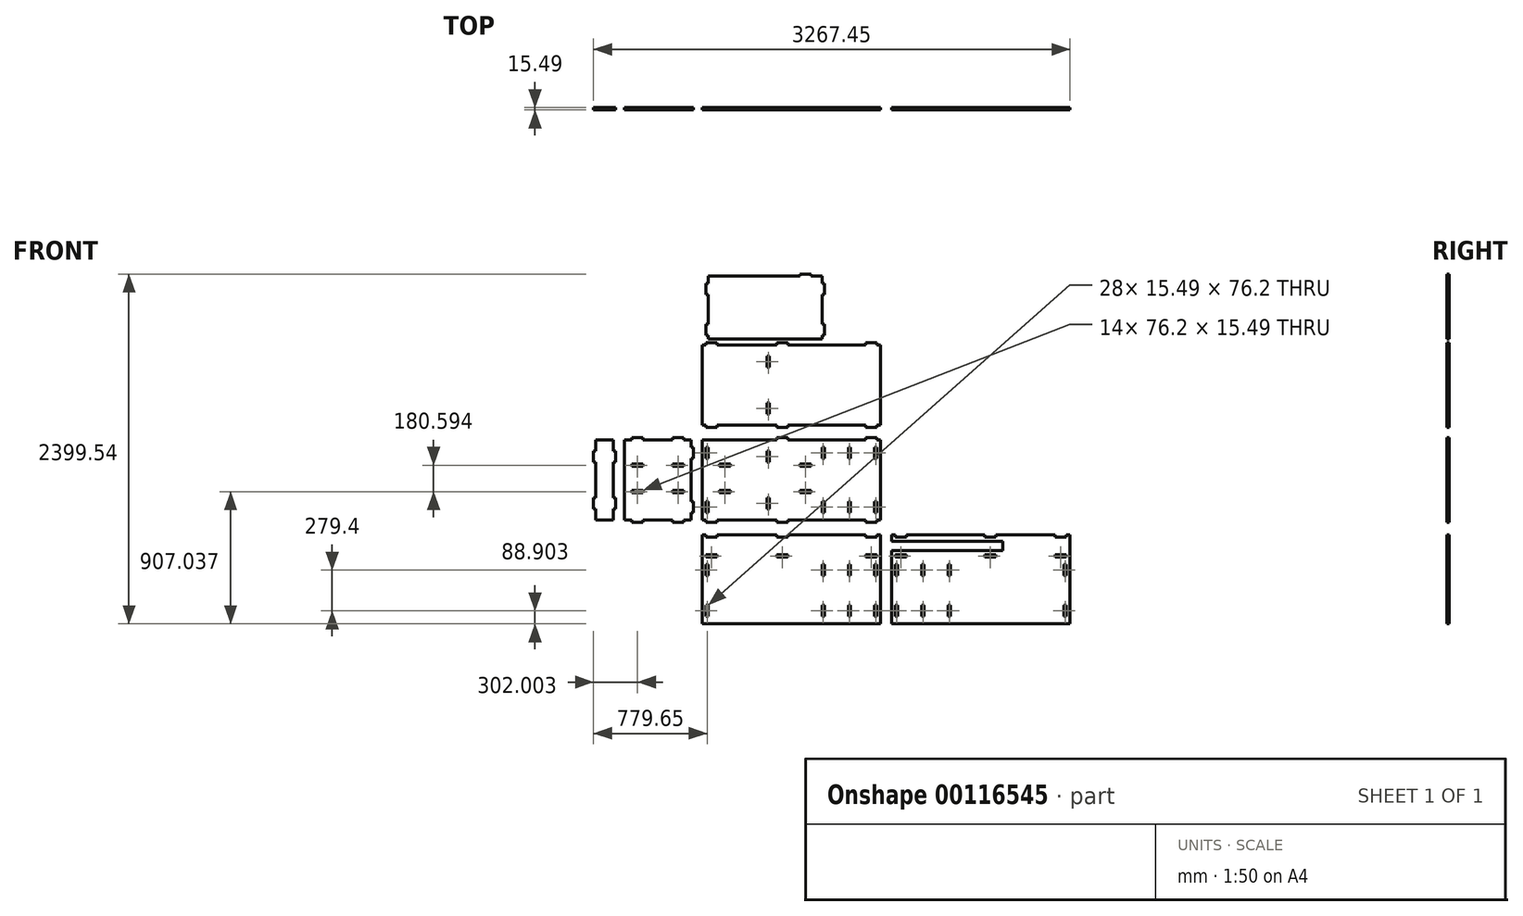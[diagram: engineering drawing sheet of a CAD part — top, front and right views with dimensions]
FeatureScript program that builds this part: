
annotation { "Feature Type Name" : "Feature", "Feature Type Description" : "" }
export const myFeature = defineFeature(function(context is Context, id is Id, definition is map)
    precondition{}
    {
        {
            var Q0;
            Q0=qCreatedBy(makeId("Front.planeOp"),FACE);
            var sketch = newSketch(context, id + "F0", { "sketchPlane" : qUnion([Q0])});
            skLineSegment(sketch, "E0.bottom", {"start": v(611.19, 274.64) * mm, "end": v(-611.19, 274.64) * mm});
            skLineSegment(sketch, "E0.top", {"start": v(611.19, -274.64) * mm, "end": v(-611.19, -274.64) * mm});
            skLineSegment(sketch, "E0.left", {"start": v(611.19, 274.64) * mm, "end": v(611.19, -274.64) * mm});
            skLineSegment(sketch, "E0.right", {"start": v(-611.19, 274.64) * mm, "end": v(-611.19, -274.64) * mm});
            skPoint(sketch, "E0.middle", {"position": v(0, 0) * mm});
            skLineSegment(sketch, "E1", {"start": v(0, 274.64) * mm, "end": v(0, -274.64) * mm, "construction": true});
            skLineSegment(sketch, "E2", {"start": v(-611.19, 0) * mm, "end": v(0, 0) * mm, "construction": true});
            skLineSegment(sketch, "E3", {"start": v(-305.6, -274.64) * mm, "end": v(-305.6, 274.64) * mm, "construction": true});
            skPoint(sketch, "E3.startSnap0", {"position": v(-305.6, 0) * mm});
            skLineSegment(sketch, "E4.bottom", {"start": v(-570.3, 223.84) * mm, "end": v(-585.79, 223.84) * mm});
            skLineSegment(sketch, "E4.top", {"start": v(-570.3, 147.64) * mm, "end": v(-585.79, 147.64) * mm});
            skLineSegment(sketch, "E4.left", {"start": v(-570.3, 223.84) * mm, "end": v(-570.3, 147.64) * mm});
            skLineSegment(sketch, "E4.right", {"start": v(-585.79, 223.84) * mm, "end": v(-585.79, 147.64) * mm});
            skLineSegment(sketch, "E5.MirrorCS", {"start": v(-570.3, -223.84) * mm, "end": v(-570.3, -147.64) * mm});
            skLineSegment(sketch, "E6.MirrorCS", {"start": v(-585.79, -223.84) * mm, "end": v(-585.79, -147.64) * mm});
            skLineSegment(sketch, "E7.MirrorCS", {"start": v(-570.3, -147.64) * mm, "end": v(-585.79, -147.64) * mm});
            skLineSegment(sketch, "E8.MirrorCS", {"start": v(-570.3, -223.84) * mm, "end": v(-585.79, -223.84) * mm});
            skLineSegment(sketch, "E9.MirrorCS", {"start": v(570.3, -223.84) * mm, "end": v(585.79, -223.84) * mm});
            skLineSegment(sketch, "E10.MirrorCS", {"start": v(570.3, -147.64) * mm, "end": v(585.79, -147.64) * mm});
            skLineSegment(sketch, "E11.MirrorCS", {"start": v(570.3, 223.84) * mm, "end": v(585.79, 223.84) * mm});
            skLineSegment(sketch, "E12.MirrorCS", {"start": v(570.3, 147.64) * mm, "end": v(585.79, 147.64) * mm});
            skLineSegment(sketch, "E13.MirrorCS", {"start": v(570.3, 223.84) * mm, "end": v(570.3, 147.64) * mm});
            skLineSegment(sketch, "E14.MirrorCS", {"start": v(585.79, 223.84) * mm, "end": v(585.79, 147.64) * mm});
            skLineSegment(sketch, "E15.MirrorCS", {"start": v(585.79, -223.84) * mm, "end": v(585.79, -147.64) * mm});
            skLineSegment(sketch, "E16.MirrorCS", {"start": v(570.3, -223.84) * mm, "end": v(570.3, -147.64) * mm});
            skLineSegment(sketch, "E17.bottom", {"start": v(-687.39, 274.64) * mm, "end": v(-1144.59, 274.64) * mm});
            skLineSegment(sketch, "E17.top", {"start": v(-687.39, -274.64) * mm, "end": v(-1144.59, -274.64) * mm});
            skLineSegment(sketch, "E17.left", {"start": v(-687.39, 274.64) * mm, "end": v(-687.39, -274.64) * mm});
            skLineSegment(sketch, "E17.right", {"start": v(-1144.59, 274.64) * mm, "end": v(-1144.59, -274.64) * mm});
            skLineSegment(sketch, "E18", {"start": v(-738.19, 274.64) * mm, "end": v(-738.19, 290.13) * mm});
            skLineSegment(sketch, "E19", {"start": v(-738.19, 290.13) * mm, "end": v(-814.39, 290.13) * mm});
            skLineSegment(sketch, "E20", {"start": v(-814.39, 290.13) * mm, "end": v(-814.39, 274.64) * mm});
            skLineSegment(sketch, "E21", {"start": v(-687.39, 223.84) * mm, "end": v(-671.9, 223.84) * mm});
            skLineSegment(sketch, "E22", {"start": v(-671.9, 223.84) * mm, "end": v(-671.9, 147.64) * mm});
            skLineSegment(sketch, "E23", {"start": v(-671.9, 147.64) * mm, "end": v(-687.39, 147.64) * mm});
            skLineSegment(sketch, "E24.MirrorCS", {"start": v(-687.39, -223.84) * mm, "end": v(-671.9, -223.84) * mm});
            skLineSegment(sketch, "E25.MirrorCS", {"start": v(-671.9, -147.64) * mm, "end": v(-687.39, -147.64) * mm});
            skLineSegment(sketch, "E26.MirrorCS", {"start": v(-671.9, -223.84) * mm, "end": v(-671.9, -147.64) * mm});
            skLineSegment(sketch, "E27", {"start": v(-915.99, 274.64) * mm, "end": v(-915.99, -274.64) * mm, "construction": true});
            skLineSegment(sketch, "E28.MirrorCS", {"start": v(-738.19, -274.64) * mm, "end": v(-738.19, -290.13) * mm});
            skLineSegment(sketch, "E29.MirrorCS", {"start": v(-814.39, -290.13) * mm, "end": v(-814.39, -274.64) * mm});
            skLineSegment(sketch, "E30.MirrorCS", {"start": v(-738.19, -290.13) * mm, "end": v(-814.39, -290.13) * mm});
            skLineSegment(sketch, "E31", {"start": v(-305.6, 223.84) * mm, "end": v(-305.6, -223.84) * mm, "construction": true});
            skPoint(sketch, "E32", {"position": v(-915.99, -279.72) * mm});
            skLineSegment(sketch, "E33.MirrorCS", {"start": v(-1017.59, -290.13) * mm, "end": v(-1017.59, -274.64) * mm});
            skLineSegment(sketch, "E34.MirrorCS", {"start": v(-1093.79, -290.13) * mm, "end": v(-1017.59, -290.13) * mm});
            skLineSegment(sketch, "E35.MirrorCS", {"start": v(-1093.79, -274.64) * mm, "end": v(-1093.79, -290.13) * mm});
            skLineSegment(sketch, "E36.MirrorCS", {"start": v(-1093.79, 274.64) * mm, "end": v(-1093.79, 290.13) * mm});
            skLineSegment(sketch, "E37.MirrorCS", {"start": v(-1093.79, 290.13) * mm, "end": v(-1017.59, 290.13) * mm});
            skLineSegment(sketch, "E38.MirrorCS", {"start": v(-1017.59, 290.13) * mm, "end": v(-1017.59, 274.64) * mm});
            skLineSegment(sketch, "E39", {"start": v(-611.19, 325.44) * mm, "end": v(611.19, 325.44) * mm, "construction": true});
            skLineSegment(sketch, "E40.MirrorCS", {"start": v(611.19, 376.24) * mm, "end": v(-611.19, 376.24) * mm});
            skLineSegment(sketch, "E41.MirrorCS", {"start": v(-611.19, 376.24) * mm, "end": v(-611.19, 925.51) * mm});
            skLineSegment(sketch, "E42.MirrorCS", {"start": v(611.19, 376.24) * mm, "end": v(611.19, 925.51) * mm});
            skLineSegment(sketch, "E43.MirrorCS", {"start": v(611.19, 925.51) * mm, "end": v(-611.19, 925.51) * mm});
            skLineSegment(sketch, "E44.bottom", {"start": v(-585.79, 274.64) * mm, "end": v(-509.59, 274.64) * mm});
            skLineSegment(sketch, "E44.top", {"start": v(-585.79, 290.13) * mm, "end": v(-509.59, 290.13) * mm});
            skLineSegment(sketch, "E44.left", {"start": v(-585.79, 274.64) * mm, "end": v(-585.79, 290.13) * mm});
            skLineSegment(sketch, "E44.right", {"start": v(-509.59, 274.64) * mm, "end": v(-509.59, 290.13) * mm});
            skLineSegment(sketch, "E45.MirrorCS", {"start": v(-25.4, 274.64) * mm, "end": v(-25.4, 290.13) * mm});
            skLineSegment(sketch, "E46.MirrorCS", {"start": v(-25.4, 290.13) * mm, "end": v(-101.6, 290.13) * mm});
            skLineSegment(sketch, "E47.MirrorCS", {"start": v(-101.6, 274.64) * mm, "end": v(-101.6, 290.13) * mm});
            skLineSegment(sketch, "E48.MirrorCS", {"start": v(585.79, 274.64) * mm, "end": v(585.79, 290.13) * mm});
            skLineSegment(sketch, "E49.MirrorCS", {"start": v(585.79, 290.13) * mm, "end": v(509.59, 290.13) * mm});
            skLineSegment(sketch, "E50.MirrorCS", {"start": v(509.59, 274.64) * mm, "end": v(509.59, 290.13) * mm});
            skLineSegment(sketch, "E51.MirrorCS", {"start": v(25.4, 274.64) * mm, "end": v(25.4, 290.13) * mm, "construction": true});
            skLineSegment(sketch, "E52.MirrorCS", {"start": v(25.4, 290.13) * mm, "end": v(101.6, 290.13) * mm, "construction": true});
            skLineSegment(sketch, "E53.MirrorCS", {"start": v(101.6, 274.64) * mm, "end": v(101.6, 290.13) * mm, "construction": true});
            skLineSegment(sketch, "E54.MirrorCS", {"start": v(-25.4, -274.64) * mm, "end": v(-25.4, -290.13) * mm});
            skLineSegment(sketch, "E55.MirrorCS", {"start": v(509.59, -274.64) * mm, "end": v(509.59, -290.13) * mm});
            skLineSegment(sketch, "E56.MirrorCS", {"start": v(585.79, -274.64) * mm, "end": v(585.79, -290.13) * mm});
            skLineSegment(sketch, "E57.MirrorCS", {"start": v(101.6, -274.64) * mm, "end": v(101.6, -290.13) * mm, "construction": true});
            skLineSegment(sketch, "E58.MirrorCS", {"start": v(25.4, -274.64) * mm, "end": v(25.4, -290.13) * mm, "construction": true});
            skLineSegment(sketch, "E59.MirrorCS", {"start": v(-101.6, -274.64) * mm, "end": v(-101.6, -290.13) * mm});
            skLineSegment(sketch, "E60.MirrorCS", {"start": v(25.4, -290.13) * mm, "end": v(101.6, -290.13) * mm, "construction": true});
            skLineSegment(sketch, "E61.MirrorCS", {"start": v(585.79, -290.13) * mm, "end": v(509.59, -290.13) * mm});
            skLineSegment(sketch, "E62.MirrorCS", {"start": v(-25.4, -290.13) * mm, "end": v(-101.6, -290.13) * mm});
            skLineSegment(sketch, "E63.MirrorCS", {"start": v(-585.79, -274.64) * mm, "end": v(-585.79, -290.13) * mm});
            skLineSegment(sketch, "E64.MirrorCS", {"start": v(-585.79, -290.13) * mm, "end": v(-509.59, -290.13) * mm});
            skLineSegment(sketch, "E65.MirrorCS", {"start": v(-509.59, -274.64) * mm, "end": v(-509.59, -290.13) * mm});
            skLineSegment(sketch, "E66.MirrorCS", {"start": v(25.4, 376.24) * mm, "end": v(25.4, 360.74) * mm, "construction": true});
            skLineSegment(sketch, "E67.MirrorCS", {"start": v(-25.4, 376.24) * mm, "end": v(-25.4, 360.74) * mm});
            skLineSegment(sketch, "E68.MirrorCS", {"start": v(101.6, 376.24) * mm, "end": v(101.6, 360.74) * mm, "construction": true});
            skLineSegment(sketch, "E69.MirrorCS", {"start": v(585.79, 376.24) * mm, "end": v(585.79, 360.74) * mm});
            skLineSegment(sketch, "E70.MirrorCS", {"start": v(509.59, 376.24) * mm, "end": v(509.59, 360.74) * mm});
            skLineSegment(sketch, "E71.MirrorCS", {"start": v(-101.6, 376.24) * mm, "end": v(-101.6, 360.74) * mm});
            skLineSegment(sketch, "E72.MirrorCS", {"start": v(-25.4, 360.74) * mm, "end": v(-101.6, 360.74) * mm});
            skLineSegment(sketch, "E73.MirrorCS", {"start": v(585.79, 360.74) * mm, "end": v(509.59, 360.74) * mm});
            skLineSegment(sketch, "E74.MirrorCS", {"start": v(25.4, 360.74) * mm, "end": v(101.6, 360.74) * mm, "construction": true});
            skLineSegment(sketch, "E75.MirrorCS", {"start": v(585.79, 925.51) * mm, "end": v(585.79, 941) * mm});
            skLineSegment(sketch, "E76.MirrorCS", {"start": v(-25.4, 925.51) * mm, "end": v(-25.4, 941) * mm});
            skLineSegment(sketch, "E77.MirrorCS", {"start": v(-101.6, 925.51) * mm, "end": v(-101.6, 941) * mm});
            skLineSegment(sketch, "E78.MirrorCS", {"start": v(-585.79, 925.51) * mm, "end": v(-585.79, 941) * mm});
            skLineSegment(sketch, "E79.MirrorCS", {"start": v(509.59, 925.51) * mm, "end": v(509.59, 941) * mm});
            skLineSegment(sketch, "E80.MirrorCS", {"start": v(-509.59, 925.51) * mm, "end": v(-509.59, 941) * mm});
            skLineSegment(sketch, "E81.MirrorCS", {"start": v(25.4, 925.51) * mm, "end": v(25.4, 941) * mm, "construction": true});
            skLineSegment(sketch, "E82.MirrorCS", {"start": v(101.6, 925.51) * mm, "end": v(101.6, 941) * mm, "construction": true});
            skLineSegment(sketch, "E83.MirrorCS", {"start": v(-25.4, 941) * mm, "end": v(-101.6, 941) * mm});
            skLineSegment(sketch, "E84.MirrorCS", {"start": v(25.4, 941) * mm, "end": v(101.6, 941) * mm, "construction": true});
            skLineSegment(sketch, "E85.MirrorCS", {"start": v(-585.79, 941) * mm, "end": v(-509.59, 941) * mm});
            skLineSegment(sketch, "E86.MirrorCS", {"start": v(585.79, 941) * mm, "end": v(509.59, 941) * mm});
            skLineSegment(sketch, "E87.MirrorCS", {"start": v(-585.79, 376.24) * mm, "end": v(-585.79, 360.74) * mm});
            skLineSegment(sketch, "E88.MirrorCS", {"start": v(-585.79, 360.74) * mm, "end": v(-509.59, 360.74) * mm});
            skLineSegment(sketch, "E89.MirrorCS", {"start": v(-509.59, 376.24) * mm, "end": v(-509.59, 360.74) * mm});
            skLineSegment(sketch, "E90", {"start": v(-150.81, 925.51) * mm, "end": v(-150.81, 376.24) * mm, "construction": true});
            skLineSegment(sketch, "E91.bottom", {"start": v(-150.81, 849.31) * mm, "end": v(-166.3, 849.31) * mm});
            skLineSegment(sketch, "E91.top", {"start": v(-150.81, 773.11) * mm, "end": v(-166.3, 773.11) * mm});
            skLineSegment(sketch, "E91.left", {"start": v(-150.81, 849.31) * mm, "end": v(-150.81, 773.11) * mm});
            skLineSegment(sketch, "E91.right", {"start": v(-166.3, 849.31) * mm, "end": v(-166.3, 773.11) * mm});
            skLineSegment(sketch, "E92", {"start": v(-611.19, 650.87) * mm, "end": v(-150.81, 650.87) * mm, "construction": true});
            skLineSegment(sketch, "E93.MirrorCS", {"start": v(-150.81, 452.44) * mm, "end": v(-166.3, 452.44) * mm});
            skLineSegment(sketch, "E94.MirrorCS", {"start": v(-150.81, 452.44) * mm, "end": v(-150.81, 528.64) * mm});
            skLineSegment(sketch, "E95.MirrorCS", {"start": v(-150.81, 528.64) * mm, "end": v(-166.3, 528.64) * mm});
            skLineSegment(sketch, "E96.MirrorCS", {"start": v(-166.3, 452.44) * mm, "end": v(-166.3, 528.64) * mm});
            skLineSegment(sketch, "E97.bottom", {"start": v(405.2, 223.84) * mm, "end": v(389.7, 223.84) * mm});
            skLineSegment(sketch, "E97.top", {"start": v(405.2, 147.64) * mm, "end": v(389.7, 147.64) * mm});
            skLineSegment(sketch, "E97.left", {"start": v(405.2, 223.84) * mm, "end": v(405.2, 147.64) * mm});
            skLineSegment(sketch, "E97.right", {"start": v(389.7, 223.84) * mm, "end": v(389.7, 147.64) * mm});
            skLineSegment(sketch, "E98.bottom", {"start": v(224.6, 223.84) * mm, "end": v(209.1, 223.84) * mm});
            skLineSegment(sketch, "E98.top", {"start": v(224.6, 147.64) * mm, "end": v(209.1, 147.64) * mm});
            skLineSegment(sketch, "E98.left", {"start": v(224.6, 223.84) * mm, "end": v(224.6, 147.64) * mm});
            skLineSegment(sketch, "E98.right", {"start": v(209.1, 223.84) * mm, "end": v(209.1, 147.64) * mm});
            skLineSegment(sketch, "E99.MirrorCS", {"start": v(224.6, -147.64) * mm, "end": v(209.1, -147.64) * mm});
            skLineSegment(sketch, "E100.MirrorCS", {"start": v(405.2, -223.84) * mm, "end": v(389.7, -223.84) * mm});
            skLineSegment(sketch, "E101.MirrorCS", {"start": v(405.2, -147.64) * mm, "end": v(389.7, -147.64) * mm});
            skLineSegment(sketch, "E102.MirrorCS", {"start": v(224.6, -223.84) * mm, "end": v(209.1, -223.84) * mm});
            skLineSegment(sketch, "E103.MirrorCS", {"start": v(209.1, -223.84) * mm, "end": v(209.1, -147.64) * mm});
            skLineSegment(sketch, "E104.MirrorCS", {"start": v(224.6, -223.84) * mm, "end": v(224.6, -147.64) * mm});
            skLineSegment(sketch, "E105.MirrorCS", {"start": v(405.2, -223.84) * mm, "end": v(405.2, -147.64) * mm});
            skLineSegment(sketch, "E106.MirrorCS", {"start": v(389.7, -223.84) * mm, "end": v(389.7, -147.64) * mm});
            skLineSegment(sketch, "E107.bottom", {"start": v(-494.1, 109.54) * mm, "end": v(-417.9, 109.54) * mm});
            skLineSegment(sketch, "E107.top", {"start": v(-494.1, 94.04) * mm, "end": v(-417.9, 94.04) * mm});
            skLineSegment(sketch, "E107.left", {"start": v(-494.1, 109.54) * mm, "end": v(-494.1, 94.04) * mm});
            skLineSegment(sketch, "E107.right", {"start": v(-417.9, 109.54) * mm, "end": v(-417.9, 94.04) * mm});
            skLineSegment(sketch, "E108", {"start": v(-570.3, 50.8) * mm, "end": v(209.1, 50.8) * mm, "construction": true});
            skLineSegment(sketch, "E109", {"start": v(-180.6, 50.8) * mm, "end": v(-180.6, 0) * mm, "construction": true});
            skLineSegment(sketch, "E110.MirrorCS", {"start": v(56.7, 109.54) * mm, "end": v(56.7, 94.04) * mm});
            skLineSegment(sketch, "E111.MirrorCS", {"start": v(132.9, 109.54) * mm, "end": v(132.9, 94.04) * mm});
            skLineSegment(sketch, "E112.MirrorCS", {"start": v(132.9, 94.04) * mm, "end": v(56.7, 94.04) * mm});
            skLineSegment(sketch, "E113.MirrorCS", {"start": v(132.9, 109.54) * mm, "end": v(56.7, 109.54) * mm});
            skLineSegment(sketch, "E114.bottom", {"start": v(-494.1, -71.06) * mm, "end": v(-417.9, -71.06) * mm});
            skLineSegment(sketch, "E114.top", {"start": v(-494.1, -86.55) * mm, "end": v(-417.9, -86.55) * mm});
            skLineSegment(sketch, "E114.left", {"start": v(-494.1, -71.06) * mm, "end": v(-494.1, -86.55) * mm});
            skLineSegment(sketch, "E114.right", {"start": v(-417.9, -71.06) * mm, "end": v(-417.9, -86.55) * mm});
            skLineSegment(sketch, "E115.MirrorCS", {"start": v(132.9, -71.06) * mm, "end": v(132.9, -86.55) * mm});
            skLineSegment(sketch, "E116.MirrorCS", {"start": v(56.7, -71.06) * mm, "end": v(56.7, -86.55) * mm});
            skLineSegment(sketch, "E117.MirrorCS", {"start": v(132.9, -71.06) * mm, "end": v(56.7, -71.06) * mm});
            skLineSegment(sketch, "E118.MirrorCS", {"start": v(132.9, -86.55) * mm, "end": v(56.7, -86.55) * mm});
            skLineSegment(sketch, "E119.bottom", {"start": v(-570.3, 966.4) * mm, "end": v(209.1, 966.4) * mm});
            skLineSegment(sketch, "E119.top", {"start": v(-570.3, 1398.2) * mm, "end": v(209.1, 1398.2) * mm});
            skLineSegment(sketch, "E119.left", {"start": v(-570.3, 966.4) * mm, "end": v(-570.3, 1398.2) * mm});
            skLineSegment(sketch, "E119.right", {"start": v(209.1, 966.4) * mm, "end": v(209.1, 1398.2) * mm});
            skLineSegment(sketch, "E120.MirrorCS", {"start": v(-150.81, 122.24) * mm, "end": v(-166.3, 122.24) * mm});
            skLineSegment(sketch, "E121.MirrorCS", {"start": v(-150.81, -198.44) * mm, "end": v(-166.3, -198.44) * mm});
            skLineSegment(sketch, "E122.MirrorCS", {"start": v(-150.81, -122.24) * mm, "end": v(-166.3, -122.24) * mm});
            skLineSegment(sketch, "E123.MirrorCS", {"start": v(-150.81, 198.44) * mm, "end": v(-166.3, 198.44) * mm});
            skLineSegment(sketch, "E124.MirrorCS", {"start": v(-150.81, -198.44) * mm, "end": v(-150.81, -122.24) * mm});
            skLineSegment(sketch, "E125.MirrorCS", {"start": v(-150.81, 198.44) * mm, "end": v(-150.81, 122.24) * mm});
            skLineSegment(sketch, "E126.MirrorCS", {"start": v(-166.3, -198.44) * mm, "end": v(-166.3, -122.24) * mm});
            skLineSegment(sketch, "E127.MirrorCS", {"start": v(-166.3, 198.44) * mm, "end": v(-166.3, 122.24) * mm});
            skLineSegment(sketch, "E128.bottom", {"start": v(-494.1, 1398.2) * mm, "end": v(-417.9, 1398.2) * mm});
            skLineSegment(sketch, "E128.top", {"start": v(-494.1, 1413.7) * mm, "end": v(-417.9, 1413.7) * mm});
            skLineSegment(sketch, "E128.left", {"start": v(-494.1, 1398.2) * mm, "end": v(-494.1, 1413.7) * mm});
            skLineSegment(sketch, "E128.right", {"start": v(-417.9, 1398.2) * mm, "end": v(-417.9, 1413.7) * mm});
            skLineSegment(sketch, "E129.MirrorCS", {"start": v(56.7, 1398.2) * mm, "end": v(56.7, 1413.7) * mm});
            skLineSegment(sketch, "E130.MirrorCS", {"start": v(132.9, 1398.2) * mm, "end": v(132.9, 1413.7) * mm});
            skLineSegment(sketch, "E131.MirrorCS", {"start": v(132.9, 1398.2) * mm, "end": v(56.7, 1398.2) * mm});
            skLineSegment(sketch, "E132.MirrorCS", {"start": v(132.9, 1413.7) * mm, "end": v(56.7, 1413.7) * mm});
            skLineSegment(sketch, "E133.bottom", {"start": v(-738.19, 109.54) * mm, "end": v(-814.39, 109.54) * mm});
            skLineSegment(sketch, "E133.top", {"start": v(-738.19, 94.04) * mm, "end": v(-814.39, 94.04) * mm});
            skLineSegment(sketch, "E133.left", {"start": v(-738.19, 109.54) * mm, "end": v(-738.19, 94.04) * mm});
            skLineSegment(sketch, "E133.right", {"start": v(-814.39, 109.54) * mm, "end": v(-814.39, 94.04) * mm});
            skLineSegment(sketch, "E134.bottom", {"start": v(-738.19, -71.06) * mm, "end": v(-814.39, -71.06) * mm});
            skLineSegment(sketch, "E134.top", {"start": v(-738.19, -86.55) * mm, "end": v(-814.39, -86.55) * mm});
            skLineSegment(sketch, "E134.left", {"start": v(-738.19, -71.06) * mm, "end": v(-738.19, -86.55) * mm});
            skLineSegment(sketch, "E134.right", {"start": v(-814.39, -71.06) * mm, "end": v(-814.39, -86.55) * mm});
            skLineSegment(sketch, "E135.bottom", {"start": v(-1017.59, 109.54) * mm, "end": v(-1093.79, 109.54) * mm});
            skLineSegment(sketch, "E135.top", {"start": v(-1017.59, 94.04) * mm, "end": v(-1093.79, 94.04) * mm});
            skLineSegment(sketch, "E135.left", {"start": v(-1017.59, 109.54) * mm, "end": v(-1017.59, 94.04) * mm});
            skLineSegment(sketch, "E135.right", {"start": v(-1093.79, 109.54) * mm, "end": v(-1093.79, 94.04) * mm});
            skLineSegment(sketch, "E136.bottom", {"start": v(-1017.59, -71.06) * mm, "end": v(-1093.79, -71.06) * mm});
            skLineSegment(sketch, "E136.top", {"start": v(-1017.59, -86.55) * mm, "end": v(-1093.79, -86.55) * mm});
            skLineSegment(sketch, "E136.left", {"start": v(-1017.59, -71.06) * mm, "end": v(-1017.59, -86.55) * mm});
            skLineSegment(sketch, "E136.right", {"start": v(-1093.79, -71.06) * mm, "end": v(-1093.79, -86.55) * mm});
            skLineSegment(sketch, "E137.bottom", {"start": v(-570.3, 1347.4) * mm, "end": v(-585.79, 1347.4) * mm});
            skLineSegment(sketch, "E137.top", {"start": v(-570.3, 1271.2) * mm, "end": v(-585.79, 1271.2) * mm});
            skLineSegment(sketch, "E137.left", {"start": v(-570.3, 1347.4) * mm, "end": v(-570.3, 1271.2) * mm});
            skLineSegment(sketch, "E137.right", {"start": v(-585.79, 1347.4) * mm, "end": v(-585.79, 1271.2) * mm});
            skLineSegment(sketch, "E138.MirrorCS", {"start": v(-570.3, 991.8) * mm, "end": v(-585.79, 991.8) * mm});
            skLineSegment(sketch, "E139.MirrorCS", {"start": v(-585.79, 991.8) * mm, "end": v(-585.79, 1068) * mm});
            skLineSegment(sketch, "E140.MirrorCS", {"start": v(-570.3, 1068) * mm, "end": v(-585.79, 1068) * mm});
            skLineSegment(sketch, "E141", {"start": v(-180.6, 1398.2) * mm, "end": v(-180.6, 966.4) * mm, "construction": true});
            skLineSegment(sketch, "E142.MirrorCS", {"start": v(209.1, 1347.4) * mm, "end": v(224.6, 1347.4) * mm});
            skLineSegment(sketch, "E143.MirrorCS", {"start": v(209.1, 1271.2) * mm, "end": v(224.6, 1271.2) * mm});
            skLineSegment(sketch, "E144.MirrorCS", {"start": v(209.1, 991.8) * mm, "end": v(224.6, 991.8) * mm});
            skLineSegment(sketch, "E145.MirrorCS", {"start": v(209.1, 1068) * mm, "end": v(224.6, 1068) * mm});
            skLineSegment(sketch, "E146.MirrorCS", {"start": v(224.6, 1347.4) * mm, "end": v(224.6, 1271.2) * mm});
            skLineSegment(sketch, "E147.MirrorCS", {"start": v(224.6, 991.8) * mm, "end": v(224.6, 1068) * mm});
            skLineSegment(sketch, "E148.MirrorCS", {"start": v(209.1, 1347.4) * mm, "end": v(209.1, 1271.2) * mm});
            skLineSegment(sketch, "E149.bottom", {"start": v(-611.19, -376.24) * mm, "end": v(611.19, -376.24) * mm});
            skLineSegment(sketch, "E149.top", {"start": v(-611.19, -985.84) * mm, "end": v(611.19, -985.84) * mm});
            skLineSegment(sketch, "E149.left", {"start": v(-611.19, -376.24) * mm, "end": v(-611.19, -985.84) * mm});
            skLineSegment(sketch, "E149.right", {"start": v(611.19, -376.24) * mm, "end": v(611.19, -985.84) * mm});
            skLineSegment(sketch, "E150", {"start": v(-611.19, -528.64) * mm, "end": v(611.19, -528.64) * mm, "construction": true});
            skLineSegment(sketch, "E151.bottom", {"start": v(-585.79, -579.44) * mm, "end": v(-570.3, -579.44) * mm});
            skLineSegment(sketch, "E151.top", {"start": v(-585.79, -655.64) * mm, "end": v(-570.3, -655.64) * mm});
            skLineSegment(sketch, "E151.left", {"start": v(-585.79, -579.44) * mm, "end": v(-585.79, -655.64) * mm});
            skLineSegment(sketch, "E151.right", {"start": v(-570.3, -579.44) * mm, "end": v(-570.3, -655.64) * mm});
            skLineSegment(sketch, "E152.bottom", {"start": v(209.1, -579.44) * mm, "end": v(224.6, -579.44) * mm});
            skLineSegment(sketch, "E152.top", {"start": v(209.1, -655.64) * mm, "end": v(224.6, -655.64) * mm});
            skLineSegment(sketch, "E152.left", {"start": v(209.1, -579.44) * mm, "end": v(209.1, -655.64) * mm});
            skLineSegment(sketch, "E152.right", {"start": v(224.6, -579.44) * mm, "end": v(224.6, -655.64) * mm});
            skLineSegment(sketch, "E153.bottom", {"start": v(389.7, -655.64) * mm, "end": v(405.2, -655.64) * mm});
            skLineSegment(sketch, "E153.top", {"start": v(389.7, -579.44) * mm, "end": v(405.2, -579.44) * mm});
            skLineSegment(sketch, "E153.left", {"start": v(389.7, -655.64) * mm, "end": v(389.7, -579.44) * mm});
            skLineSegment(sketch, "E153.right", {"start": v(405.2, -655.64) * mm, "end": v(405.2, -579.44) * mm});
            skLineSegment(sketch, "E154.bottom", {"start": v(570.3, -655.64) * mm, "end": v(585.79, -655.64) * mm});
            skLineSegment(sketch, "E154.top", {"start": v(570.3, -579.44) * mm, "end": v(585.79, -579.44) * mm});
            skLineSegment(sketch, "E154.left", {"start": v(570.3, -655.64) * mm, "end": v(570.3, -579.44) * mm});
            skLineSegment(sketch, "E154.right", {"start": v(585.79, -655.64) * mm, "end": v(585.79, -579.44) * mm});
            skLineSegment(sketch, "E155", {"start": v(0, -528.64) * mm, "end": v(0, -985.84) * mm, "construction": true});
            skLineSegment(sketch, "E156", {"start": v(0, -757.24) * mm, "end": v(611.19, -757.24) * mm, "construction": true});
            skLineSegment(sketch, "E157.MirrorCS", {"start": v(389.7, -858.84) * mm, "end": v(405.2, -858.84) * mm});
            skLineSegment(sketch, "E158.MirrorCS", {"start": v(209.1, -935.04) * mm, "end": v(224.6, -935.04) * mm});
            skLineSegment(sketch, "E159.MirrorCS", {"start": v(-585.79, -858.84) * mm, "end": v(-570.3, -858.84) * mm});
            skLineSegment(sketch, "E160.MirrorCS", {"start": v(570.3, -935.04) * mm, "end": v(585.79, -935.04) * mm});
            skLineSegment(sketch, "E161.MirrorCS", {"start": v(389.7, -935.04) * mm, "end": v(405.2, -935.04) * mm});
            skLineSegment(sketch, "E162.MirrorCS", {"start": v(209.1, -858.84) * mm, "end": v(224.6, -858.84) * mm});
            skLineSegment(sketch, "E163.MirrorCS", {"start": v(-585.79, -935.04) * mm, "end": v(-570.3, -935.04) * mm});
            skLineSegment(sketch, "E164.MirrorCS", {"start": v(570.3, -858.84) * mm, "end": v(585.79, -858.84) * mm});
            skLineSegment(sketch, "E165.MirrorCS", {"start": v(224.6, -935.04) * mm, "end": v(224.6, -858.84) * mm});
            skLineSegment(sketch, "E166.MirrorCS", {"start": v(-570.3, -935.04) * mm, "end": v(-570.3, -858.84) * mm});
            skLineSegment(sketch, "E167.MirrorCS", {"start": v(389.7, -858.84) * mm, "end": v(389.7, -935.04) * mm});
            skLineSegment(sketch, "E168.MirrorCS", {"start": v(-585.79, -935.04) * mm, "end": v(-585.79, -858.84) * mm});
            skLineSegment(sketch, "E169.MirrorCS", {"start": v(585.79, -858.84) * mm, "end": v(585.79, -935.04) * mm});
            skLineSegment(sketch, "E170.MirrorCS", {"start": v(405.2, -858.84) * mm, "end": v(405.2, -935.04) * mm});
            skLineSegment(sketch, "E171.MirrorCS", {"start": v(570.3, -858.84) * mm, "end": v(570.3, -935.04) * mm});
            skLineSegment(sketch, "E172.MirrorCS", {"start": v(209.1, -935.04) * mm, "end": v(209.1, -858.84) * mm});
            skLineSegment(sketch, "E173", {"start": v(649.29, -376.24) * mm, "end": v(649.29, -985.84) * mm, "construction": true});
            skLineSegment(sketch, "E174.MirrorCS", {"start": v(908.88, -655.64) * mm, "end": v(893.38, -655.64) * mm});
            skLineSegment(sketch, "E175.MirrorCS", {"start": v(728.28, -935.04) * mm, "end": v(712.79, -935.04) * mm});
            skLineSegment(sketch, "E176.MirrorCS", {"start": v(1089.47, -655.64) * mm, "end": v(1073.98, -655.64) * mm});
            skLineSegment(sketch, "E177.MirrorCS", {"start": v(1884.36, -858.84) * mm, "end": v(1868.87, -858.84) * mm});
            skLineSegment(sketch, "E178.MirrorCS", {"start": v(1089.47, -579.44) * mm, "end": v(1073.98, -579.44) * mm});
            skLineSegment(sketch, "E179.MirrorCS", {"start": v(908.88, -858.84) * mm, "end": v(893.38, -858.84) * mm});
            skLineSegment(sketch, "E180.MirrorCS", {"start": v(1089.47, -858.84) * mm, "end": v(1073.98, -858.84) * mm});
            skLineSegment(sketch, "E181.MirrorCS", {"start": v(908.88, -579.44) * mm, "end": v(893.38, -579.44) * mm});
            skLineSegment(sketch, "E182.MirrorCS", {"start": v(728.28, -655.64) * mm, "end": v(712.79, -655.64) * mm});
            skLineSegment(sketch, "E183.MirrorCS", {"start": v(1884.36, -655.64) * mm, "end": v(1868.87, -655.64) * mm});
            skLineSegment(sketch, "E184.MirrorCS", {"start": v(728.28, -858.84) * mm, "end": v(712.79, -858.84) * mm});
            skLineSegment(sketch, "E185.MirrorCS", {"start": v(728.28, -579.44) * mm, "end": v(712.79, -579.44) * mm});
            skLineSegment(sketch, "E186.MirrorCS", {"start": v(1884.36, -579.44) * mm, "end": v(1868.87, -579.44) * mm});
            skLineSegment(sketch, "E187.MirrorCS", {"start": v(908.88, -935.04) * mm, "end": v(893.38, -935.04) * mm});
            skLineSegment(sketch, "E188.MirrorCS", {"start": v(1884.36, -935.04) * mm, "end": v(1868.87, -935.04) * mm});
            skLineSegment(sketch, "E189.MirrorCS", {"start": v(1089.47, -935.04) * mm, "end": v(1073.98, -935.04) * mm});
            skLineSegment(sketch, "E190.MirrorCS", {"start": v(1909.76, -376.24) * mm, "end": v(687.39, -376.24) * mm});
            skLineSegment(sketch, "E191.MirrorCS", {"start": v(1884.36, -579.44) * mm, "end": v(1884.36, -655.64) * mm});
            skLineSegment(sketch, "E192.MirrorCS", {"start": v(1298.57, -528.64) * mm, "end": v(1298.57, -985.84) * mm, "construction": true});
            skLineSegment(sketch, "E193.MirrorCS", {"start": v(728.28, -858.84) * mm, "end": v(728.28, -935.04) * mm});
            skLineSegment(sketch, "E194.MirrorCS", {"start": v(908.88, -655.64) * mm, "end": v(908.88, -579.44) * mm});
            skLineSegment(sketch, "E195.MirrorCS", {"start": v(1909.76, -528.64) * mm, "end": v(687.39, -528.64) * mm, "construction": true});
            skLineSegment(sketch, "E196.MirrorCS", {"start": v(712.79, -655.64) * mm, "end": v(712.79, -579.44) * mm});
            skLineSegment(sketch, "E197.MirrorCS", {"start": v(893.38, -858.84) * mm, "end": v(893.38, -935.04) * mm});
            skLineSegment(sketch, "E198.MirrorCS", {"start": v(1073.98, -935.04) * mm, "end": v(1073.98, -858.84) * mm});
            skLineSegment(sketch, "E199.MirrorCS", {"start": v(1909.76, -985.84) * mm, "end": v(687.39, -985.84) * mm});
            skLineSegment(sketch, "E200.MirrorCS", {"start": v(1868.87, -935.04) * mm, "end": v(1868.87, -858.84) * mm});
            skLineSegment(sketch, "E201.MirrorCS", {"start": v(1884.36, -935.04) * mm, "end": v(1884.36, -858.84) * mm});
            skLineSegment(sketch, "E202.MirrorCS", {"start": v(1089.47, -935.04) * mm, "end": v(1089.47, -858.84) * mm});
            skLineSegment(sketch, "E203.MirrorCS", {"start": v(1073.98, -579.44) * mm, "end": v(1073.98, -655.64) * mm});
            skLineSegment(sketch, "E204.MirrorCS", {"start": v(1909.76, -376.24) * mm, "end": v(1909.76, -985.84) * mm});
            skLineSegment(sketch, "E205.MirrorCS", {"start": v(728.28, -655.64) * mm, "end": v(728.28, -579.44) * mm});
            skLineSegment(sketch, "E206.MirrorCS", {"start": v(1298.57, -757.24) * mm, "end": v(687.39, -757.24) * mm, "construction": true});
            skLineSegment(sketch, "E207.MirrorCS", {"start": v(908.88, -858.84) * mm, "end": v(908.88, -935.04) * mm});
            skLineSegment(sketch, "E208.MirrorCS", {"start": v(1089.47, -579.44) * mm, "end": v(1089.47, -655.64) * mm});
            skLineSegment(sketch, "E209.MirrorCS", {"start": v(893.38, -655.64) * mm, "end": v(893.38, -579.44) * mm});
            skLineSegment(sketch, "E210.MirrorCS", {"start": v(1868.87, -579.44) * mm, "end": v(1868.87, -655.64) * mm});
            skLineSegment(sketch, "E211.MirrorCS", {"start": v(712.79, -858.84) * mm, "end": v(712.79, -935.04) * mm});
            skLineSegment(sketch, "E212.MirrorCS", {"start": v(687.39, -376.24) * mm, "end": v(687.39, -985.84) * mm});
            skLineSegment(sketch, "E213", {"start": v(687.39, -420.69) * mm, "end": v(1449.39, -420.69) * mm});
            skLineSegment(sketch, "E214", {"start": v(1449.39, -420.69) * mm, "end": v(1449.39, -484.19) * mm});
            skLineSegment(sketch, "E215", {"start": v(0, -274.64) * mm, "end": v(0, -528.64) * mm, "construction": true});
            skLineSegment(sketch, "E216", {"start": v(0, -401.64) * mm, "end": v(-25.4, -401.64) * mm, "construction": true});
            skLineSegment(sketch, "E217.MirrorCS", {"start": v(-25.4, -528.64) * mm, "end": v(-25.4, -513.14) * mm});
            skLineSegment(sketch, "E218.MirrorCS", {"start": v(-509.59, -528.64) * mm, "end": v(-509.59, -513.14) * mm});
            skLineSegment(sketch, "E219.MirrorCS", {"start": v(-101.6, -528.64) * mm, "end": v(-101.6, -513.14) * mm});
            skLineSegment(sketch, "E220.MirrorCS", {"start": v(-585.79, -528.64) * mm, "end": v(-585.79, -513.14) * mm});
            skLineSegment(sketch, "E221.MirrorCS", {"start": v(-585.79, -513.14) * mm, "end": v(-509.59, -513.14) * mm});
            skLineSegment(sketch, "E222.MirrorCS", {"start": v(-25.4, -513.14) * mm, "end": v(-101.6, -513.14) * mm});
            skLineSegment(sketch, "E223.MirrorCS", {"start": v(585.79, -528.64) * mm, "end": v(585.79, -513.14) * mm});
            skLineSegment(sketch, "E224.MirrorCS", {"start": v(509.59, -528.64) * mm, "end": v(509.59, -513.14) * mm});
            skLineSegment(sketch, "E225.MirrorCS", {"start": v(585.79, -513.14) * mm, "end": v(509.59, -513.14) * mm});
            skLineSegment(sketch, "E226", {"start": v(509.59, -528.64) * mm, "end": v(585.79, -528.64) * mm});
            skLineSegment(sketch, "E227", {"start": v(-101.6, -528.64) * mm, "end": v(-25.4, -528.64) * mm});
            skLineSegment(sketch, "E228", {"start": v(-585.79, -528.64) * mm, "end": v(-509.59, -528.64) * mm});
            skLineSegment(sketch, "E229.MirrorCS", {"start": v(788.99, -528.64) * mm, "end": v(712.79, -528.64) * mm});
            skLineSegment(sketch, "E230.MirrorCS", {"start": v(712.79, -513.14) * mm, "end": v(788.99, -513.14) * mm});
            skLineSegment(sketch, "E231.MirrorCS", {"start": v(712.79, -528.64) * mm, "end": v(712.79, -513.14) * mm});
            skLineSegment(sketch, "E232.MirrorCS", {"start": v(788.99, -528.64) * mm, "end": v(788.99, -513.14) * mm});
            skLineSegment(sketch, "E233.MirrorCS", {"start": v(1323.98, -528.64) * mm, "end": v(1323.98, -513.14) * mm});
            skLineSegment(sketch, "E234.MirrorCS", {"start": v(1400.18, -528.64) * mm, "end": v(1400.18, -513.14) * mm});
            skLineSegment(sketch, "E235.MirrorCS", {"start": v(1400.18, -528.64) * mm, "end": v(1323.98, -528.64) * mm});
            skLineSegment(sketch, "E236.MirrorCS", {"start": v(1323.97, -513.14) * mm, "end": v(1400.17, -513.14) * mm});
            skLineSegment(sketch, "E237.MirrorCS", {"start": v(1884.36, -513.14) * mm, "end": v(1808.16, -513.14) * mm});
            skLineSegment(sketch, "E238.MirrorCS", {"start": v(1808.16, -528.64) * mm, "end": v(1808.16, -513.14) * mm});
            skLineSegment(sketch, "E239.MirrorCS", {"start": v(1884.36, -528.64) * mm, "end": v(1808.16, -528.64) * mm});
            skLineSegment(sketch, "E240.MirrorCS", {"start": v(1884.36, -528.64) * mm, "end": v(1884.36, -513.14) * mm});
            skLineSegment(sketch, "E241", {"start": v(687.39, -484.19) * mm, "end": v(1449.39, -484.19) * mm});
            skLineSegment(sketch, "E242.bottom", {"start": v(-1220.79, -274.64) * mm, "end": v(-1342.2, -274.64) * mm});
            skLineSegment(sketch, "E242.top", {"start": v(-1220.79, 274.64) * mm, "end": v(-1342.2, 274.64) * mm});
            skLineSegment(sketch, "E242.left", {"start": v(-1220.79, -274.64) * mm, "end": v(-1220.79, 274.64) * mm});
            skLineSegment(sketch, "E242.right", {"start": v(-1342.2, -274.64) * mm, "end": v(-1342.2, 274.64) * mm});
            skPoint(sketch, "E243.oppositeSnap0", {"position": v(-679.64, 223.84) * mm});
            skLineSegment(sketch, "E244", {"start": v(-25.4, -376.24) * mm, "end": v(-25.4, -528.64) * mm, "construction": true});
            skLineSegment(sketch, "E245", {"start": v(-25.4, -452.44) * mm, "end": v(0, -452.44) * mm, "construction": true});
            skLineSegment(sketch, "E246.MirrorCS", {"start": v(-585.79, -376.24) * mm, "end": v(-585.79, -391.73) * mm});
            skLineSegment(sketch, "E247.MirrorCS", {"start": v(-101.6, -376.24) * mm, "end": v(-101.6, -391.73) * mm});
            skLineSegment(sketch, "E248.MirrorCS", {"start": v(-509.59, -376.24) * mm, "end": v(-509.59, -391.73) * mm});
            skLineSegment(sketch, "E249.MirrorCS", {"start": v(-25.4, -376.24) * mm, "end": v(-25.4, -391.73) * mm});
            skLineSegment(sketch, "E250.MirrorCS", {"start": v(509.59, -376.24) * mm, "end": v(509.59, -391.73) * mm});
            skLineSegment(sketch, "E251.MirrorCS", {"start": v(585.79, -376.24) * mm, "end": v(585.79, -391.73) * mm});
            skLineSegment(sketch, "E252.MirrorCS", {"start": v(-585.79, -391.73) * mm, "end": v(-509.59, -391.73) * mm});
            skLineSegment(sketch, "E253.MirrorCS", {"start": v(-585.79, -376.24) * mm, "end": v(-509.59, -376.24) * mm});
            skLineSegment(sketch, "E254.MirrorCS", {"start": v(-101.6, -376.24) * mm, "end": v(-25.4, -376.24) * mm});
            skLineSegment(sketch, "E255.MirrorCS", {"start": v(509.59, -376.24) * mm, "end": v(585.79, -376.24) * mm});
            skLineSegment(sketch, "E256.MirrorCS", {"start": v(585.79, -391.73) * mm, "end": v(509.59, -391.73) * mm});
            skLineSegment(sketch, "E257.MirrorCS", {"start": v(-25.4, -391.73) * mm, "end": v(-101.6, -391.73) * mm});
            skLineSegment(sketch, "E258.MirrorCS", {"start": v(1400.18, -376.24) * mm, "end": v(1400.18, -391.73) * mm});
            skLineSegment(sketch, "E259.MirrorCS", {"start": v(1323.98, -376.24) * mm, "end": v(1323.98, -391.73) * mm});
            skLineSegment(sketch, "E260.MirrorCS", {"start": v(788.99, -376.24) * mm, "end": v(788.99, -391.73) * mm});
            skLineSegment(sketch, "E261.MirrorCS", {"start": v(712.79, -376.24) * mm, "end": v(712.79, -391.73) * mm});
            skLineSegment(sketch, "E262.MirrorCS", {"start": v(1884.36, -376.24) * mm, "end": v(1884.36, -391.73) * mm});
            skLineSegment(sketch, "E263.MirrorCS", {"start": v(1808.16, -376.24) * mm, "end": v(1808.16, -391.73) * mm});
            skLineSegment(sketch, "E264.MirrorCS", {"start": v(1884.36, -391.73) * mm, "end": v(1808.16, -391.73) * mm});
            skLineSegment(sketch, "E265.MirrorCS", {"start": v(1323.97, -391.73) * mm, "end": v(1400.17, -391.73) * mm});
            skLineSegment(sketch, "E266.MirrorCS", {"start": v(1400.18, -376.24) * mm, "end": v(1323.98, -376.24) * mm});
            skLineSegment(sketch, "E267.MirrorCS", {"start": v(712.79, -391.73) * mm, "end": v(788.99, -391.73) * mm});
            skLineSegment(sketch, "E268.MirrorCS", {"start": v(788.99, -376.24) * mm, "end": v(712.79, -376.24) * mm});
            skLineSegment(sketch, "E269.MirrorCS", {"start": v(1884.36, -376.24) * mm, "end": v(1808.16, -376.24) * mm});
            skLineSegment(sketch, "E270.bottom", {"start": v(-1220.79, 198.44) * mm, "end": v(-1205.3, 198.44) * mm});
            skLineSegment(sketch, "E270.top", {"start": v(-1220.79, 122.24) * mm, "end": v(-1205.3, 122.24) * mm});
            skLineSegment(sketch, "E270.left", {"start": v(-1220.79, 198.44) * mm, "end": v(-1220.79, 122.24) * mm});
            skLineSegment(sketch, "E270.right", {"start": v(-1205.3, 198.44) * mm, "end": v(-1205.3, 122.24) * mm});
            skLineSegment(sketch, "E271.bottom", {"start": v(-1220.79, -122.24) * mm, "end": v(-1205.3, -122.24) * mm});
            skLineSegment(sketch, "E271.top", {"start": v(-1220.79, -198.44) * mm, "end": v(-1205.3, -198.44) * mm});
            skLineSegment(sketch, "E271.left", {"start": v(-1220.79, -122.24) * mm, "end": v(-1220.79, -198.44) * mm});
            skLineSegment(sketch, "E271.right", {"start": v(-1205.3, -122.24) * mm, "end": v(-1205.3, -198.44) * mm});
            skLineSegment(sketch, "E272", {"start": v(-1281.5, 274.64) * mm, "end": v(-1281.5, -274.64) * mm, "construction": true});
            skLineSegment(sketch, "E273.MirrorCS", {"start": v(-1342.2, 122.24) * mm, "end": v(-1357.7, 122.24) * mm});
            skLineSegment(sketch, "E274.MirrorCS", {"start": v(-1342.2, 198.44) * mm, "end": v(-1357.7, 198.44) * mm});
            skLineSegment(sketch, "E275.MirrorCS", {"start": v(-1342.2, -198.44) * mm, "end": v(-1357.7, -198.44) * mm});
            skLineSegment(sketch, "E276.MirrorCS", {"start": v(-1342.2, -122.24) * mm, "end": v(-1357.7, -122.24) * mm});
            skLineSegment(sketch, "E277.MirrorCS", {"start": v(-1357.7, 198.44) * mm, "end": v(-1357.7, 122.24) * mm});
            skLineSegment(sketch, "E278.MirrorCS", {"start": v(-1342.2, 198.44) * mm, "end": v(-1342.2, 122.24) * mm});
            skLineSegment(sketch, "E279.MirrorCS", {"start": v(-1357.7, -122.24) * mm, "end": v(-1357.7, -198.44) * mm});
            skLineSegment(sketch, "E280.MirrorCS", {"start": v(-1342.2, -122.24) * mm, "end": v(-1342.2, -198.44) * mm});
            skSolve(sketch);
        }
        {
            var Q0;
            Q0=makeQuery(id+"F0.imprint","IMPRINT",FACE,{"disambiguationData":[TD([[makeQuery(id+"F0.imprint","IMPRINT",EDGE,{"derivedFrom":sQuery(id+"F0.wireOp",EDGE,"E174.MirrorCS")}),1.0]])]});
            var Q1;
            Q1=makeQuery(id+"F0.imprint","IMPRINT",FACE,{"disambiguationData":[TD([[makeQuery(id+"F0.imprint","IMPRINT",EDGE,{"derivedFrom":sQuery(id+"F0.wireOp",EDGE,"E149.bottom")}),-1.0]])]});
            var Q2;
            {var subQ6=sQuery(id+"F0.wireOp",EDGE,"E41.MirrorCS");Q2=makeQuery(id+"F0.imprint","IMPRINT",FACE,{"disambiguationData":[TD([[makeQuery(id+"F0.imprint","IMPRINT",EDGE,{"derivedFrom":subQ6}),-1.0]])]});}
            var Q3;
            {var subQ7=sQuery(id+"F0.wireOp",EDGE,"E0.left");Q3=makeQuery(id+"F0.imprint","IMPRINT",FACE,{"disambiguationData":[TD([[makeQuery(id+"F0.imprint","IMPRINT",EDGE,{"derivedFrom":subQ7}),-1.0]])]});}
            var Q4;
            {var subQ11=sQuery(id+"F0.wireOp",EDGE,"E17.right");Q4=makeQuery(id+"F0.imprint","IMPRINT",FACE,{"disambiguationData":[TD([[makeQuery(id+"F0.imprint","IMPRINT",EDGE,{"derivedFrom":subQ11}),1.0]])]});}
            var Q5;
            {var subQ2=sQuery(id+"F0.wireOp",EDGE,"E242.bottom");Q5=makeQuery(id+"F0.imprint","IMPRINT",FACE,{"disambiguationData":[TD([[makeQuery(id+"F0.imprint","IMPRINT",EDGE,{"derivedFrom":subQ2}),-1.0]])]});}
            var Q6;
            {var subQ0=sQuery(id+"F0.wireOp",EDGE,"E24.MirrorCS");Q6=makeQuery(id+"F0.imprint","IMPRINT",FACE,{"disambiguationData":[TD([[makeQuery(id+"F0.imprint","IMPRINT",EDGE,{"derivedFrom":subQ0}),1.0]])]});}
            var Q7;
            {var subQ0=sQuery(id+"F0.wireOp",EDGE,"E28.MirrorCS");Q7=makeQuery(id+"F0.imprint","IMPRINT",FACE,{"disambiguationData":[TD([[makeQuery(id+"F0.imprint","IMPRINT",EDGE,{"derivedFrom":subQ0}),-1.0]])]});}
            var Q8;
            {var subQ0=sQuery(id+"F0.wireOp",EDGE,"E33.MirrorCS");Q8=makeQuery(id+"F0.imprint","IMPRINT",FACE,{"disambiguationData":[TD([[makeQuery(id+"F0.imprint","IMPRINT",EDGE,{"derivedFrom":subQ0}),1.0]])]});}
            var Q9;
            Q9=makeQuery(id+"F0.imprint","IMPRINT",FACE,{"disambiguationData":[TD([[makeQuery(id+"F0.imprint","IMPRINT",EDGE,{"derivedFrom":sQuery(id+"F0.wireOp",EDGE,"aYnf5qZs-QdGl-farf-CuMQ-HYCGy644belK.bottom")}),1.0]])]});
            var Q10;
            {var subQ0=sQuery(id+"F0.wireOp",EDGE,"E63.MirrorCS");Q10=makeQuery(id+"F0.imprint","IMPRINT",FACE,{"disambiguationData":[TD([[makeQuery(id+"F0.imprint","IMPRINT",EDGE,{"derivedFrom":subQ0}),1.0]])]});}
            var Q11;
            {var subQ0=sQuery(id+"F0.wireOp",EDGE,"E54.MirrorCS");Q11=makeQuery(id+"F0.imprint","IMPRINT",FACE,{"disambiguationData":[TD([[makeQuery(id+"F0.imprint","IMPRINT",EDGE,{"derivedFrom":subQ0}),-1.0]])]});}
            var Q12;
            Q12=makeQuery(id+"F0.imprint","IMPRINT",FACE,{"disambiguationData":[TD([[makeQuery(id+"F0.imprint","IMPRINT",EDGE,{"derivedFrom":sQuery(id+"F0.wireOp",EDGE,"gmpWObY7-QqzQ-WBJT-4Goy-TdPHXSVDOevC.bottom")}),-1.0]])]});
            var Q13;
            Q13=makeQuery(id+"F0.imprint","IMPRINT",FACE,{"disambiguationData":[TD([[makeQuery(id+"F0.imprint","IMPRINT",EDGE,{"derivedFrom":sQuery(id+"F0.wireOp",EDGE,"innGTp8h-KEVj-rHjC-CBeV-Cfe61kPgFdgl.bottom")}),-1.0]])]});
            var Q14;
            Q14=makeQuery(id+"F0.imprint","IMPRINT",FACE,{"disambiguationData":[TD([[makeQuery(id+"F0.imprint","IMPRINT",EDGE,{"derivedFrom":sQuery(id+"F0.wireOp",EDGE,"E243.bottom")}),1.0]])]});
            var Q15;
            {var subQ0=sQuery(id+"F0.wireOp",EDGE,"E36.MirrorCS");Q15=makeQuery(id+"F0.imprint","IMPRINT",FACE,{"disambiguationData":[TD([[makeQuery(id+"F0.imprint","IMPRINT",EDGE,{"derivedFrom":subQ0}),-1.0]])]});}
            var Q16;
            {var subQ0=sQuery(id+"F0.wireOp",EDGE,"E18");Q16=makeQuery(id+"F0.imprint","IMPRINT",FACE,{"disambiguationData":[TD([[makeQuery(id+"F0.imprint","IMPRINT",EDGE,{"derivedFrom":subQ0}),1.0]])]});}
            var Q17;
            {var subQ0=sQuery(id+"F0.wireOp",EDGE,"E21");Q17=makeQuery(id+"F0.imprint","IMPRINT",FACE,{"disambiguationData":[TD([[makeQuery(id+"F0.imprint","IMPRINT",EDGE,{"derivedFrom":subQ0}),-1.0]])]});}
            var Q18;
            Q18=makeQuery(id+"F0.imprint","IMPRINT",FACE,{"disambiguationData":[TD([[makeQuery(id+"F0.imprint","IMPRINT",EDGE,{"derivedFrom":sQuery(id+"F0.wireOp",EDGE,"E44.bottom")}),1.0]])]});
            var Q19;
            {var subQ0=sQuery(id+"F0.wireOp",EDGE,"E87.MirrorCS");Q19=makeQuery(id+"F0.imprint","IMPRINT",FACE,{"disambiguationData":[TD([[makeQuery(id+"F0.imprint","IMPRINT",EDGE,{"derivedFrom":subQ0}),1.0]])]});}
            var Q20;
            {var subQ0=sQuery(id+"F0.wireOp",EDGE,"E67.MirrorCS");Q20=makeQuery(id+"F0.imprint","IMPRINT",FACE,{"disambiguationData":[TD([[makeQuery(id+"F0.imprint","IMPRINT",EDGE,{"derivedFrom":subQ0}),-1.0]])]});}
            var Q21;
            {var subQ0=sQuery(id+"F0.wireOp",EDGE,"E45.MirrorCS");Q21=makeQuery(id+"F0.imprint","IMPRINT",FACE,{"disambiguationData":[TD([[makeQuery(id+"F0.imprint","IMPRINT",EDGE,{"derivedFrom":subQ0}),1.0]])]});}
            var Q22;
            {var subQ0=sQuery(id+"F0.wireOp",EDGE,"E69.MirrorCS");Q22=makeQuery(id+"F0.imprint","IMPRINT",FACE,{"disambiguationData":[TD([[makeQuery(id+"F0.imprint","IMPRINT",EDGE,{"derivedFrom":subQ0}),-1.0]])]});}
            var Q23;
            {var subQ0=sQuery(id+"F0.wireOp",EDGE,"E48.MirrorCS");Q23=makeQuery(id+"F0.imprint","IMPRINT",FACE,{"disambiguationData":[TD([[makeQuery(id+"F0.imprint","IMPRINT",EDGE,{"derivedFrom":subQ0}),1.0]])]});}
            var Q24;
            {var subQ0=sQuery(id+"F0.wireOp",EDGE,"E55.MirrorCS");Q24=makeQuery(id+"F0.imprint","IMPRINT",FACE,{"disambiguationData":[TD([[makeQuery(id+"F0.imprint","IMPRINT",EDGE,{"derivedFrom":subQ0}),1.0]])]});}
            var Q25;
            {var subQ1=sQuery(id+"F0.wireOp",EDGE,"E119.bottom");Q25=makeQuery(id+"F0.imprint","IMPRINT",FACE,{"disambiguationData":[TD([[makeQuery(id+"F0.imprint","IMPRINT",EDGE,{"derivedFrom":subQ1}),1.0]])]});}
            var Q26;
            Q26=makeQuery(id+"F0.imprint","IMPRINT",FACE,{"disambiguationData":[TD([[makeQuery(id+"F0.imprint","IMPRINT",EDGE,{"derivedFrom":sQuery(id+"F0.wireOp",EDGE,"E128.bottom")}),1.0]])]});
            var Q27;
            Q27=makeQuery(id+"F0.imprint","IMPRINT",FACE,{"disambiguationData":[TD([[makeQuery(id+"F0.imprint","IMPRINT",EDGE,{"derivedFrom":sQuery(id+"F0.wireOp",EDGE,"E137.bottom")}),1.0]])]});
            var Q28;
            {var subQ0=sQuery(id+"F0.wireOp",EDGE,"E138.MirrorCS");Q28=makeQuery(id+"F0.imprint","IMPRINT",FACE,{"disambiguationData":[TD([[makeQuery(id+"F0.imprint","IMPRINT",EDGE,{"derivedFrom":subQ0}),-1.0]])]});}
            var Q29;
            Q29=makeQuery(id+"F0.imprint","IMPRINT",FACE,{"disambiguationData":[TD([[makeQuery(id+"F0.imprint","IMPRINT",EDGE,{"derivedFrom":sQuery(id+"F0.wireOp",EDGE,"E129.MirrorCS")}),-1.0]])]});
            var Q30;
            Q30=makeQuery(id+"F0.imprint","IMPRINT",FACE,{"disambiguationData":[TD([[makeQuery(id+"F0.imprint","IMPRINT",EDGE,{"derivedFrom":sQuery(id+"F0.wireOp",EDGE,"E142.MirrorCS")}),-1.0]])]});
            var Q31;
            {var subQ0=sQuery(id+"F0.wireOp",EDGE,"E144.MirrorCS");Q31=makeQuery(id+"F0.imprint","IMPRINT",FACE,{"disambiguationData":[TD([[makeQuery(id+"F0.imprint","IMPRINT",EDGE,{"derivedFrom":subQ0}),1.0]])]});}
            var Q32;
            {var subQ0=sQuery(id+"F0.wireOp",EDGE,"E75.MirrorCS");Q32=makeQuery(id+"F0.imprint","IMPRINT",FACE,{"disambiguationData":[TD([[makeQuery(id+"F0.imprint","IMPRINT",EDGE,{"derivedFrom":subQ0}),1.0]])]});}
            var Q33;
            {var subQ0=sQuery(id+"F0.wireOp",EDGE,"E76.MirrorCS");Q33=makeQuery(id+"F0.imprint","IMPRINT",FACE,{"disambiguationData":[TD([[makeQuery(id+"F0.imprint","IMPRINT",EDGE,{"derivedFrom":subQ0}),1.0]])]});}
            var Q34;
            {var subQ0=sQuery(id+"F0.wireOp",EDGE,"E78.MirrorCS");Q34=makeQuery(id+"F0.imprint","IMPRINT",FACE,{"disambiguationData":[TD([[makeQuery(id+"F0.imprint","IMPRINT",EDGE,{"derivedFrom":subQ0}),-1.0]])]});}
            var Q35;
            Q35=makeQuery(id+"F0.imprint","IMPRINT",FACE,{"disambiguationData":[TD([[makeQuery(id+"F0.imprint","IMPRINT",EDGE,{"derivedFrom":sQuery(id+"F0.wireOp",EDGE,"E273.MirrorCS")}),-1.0]])]});
            var Q36;
            Q36=makeQuery(id+"F0.imprint","IMPRINT",FACE,{"disambiguationData":[TD([[makeQuery(id+"F0.imprint","IMPRINT",EDGE,{"derivedFrom":sQuery(id+"F0.wireOp",EDGE,"E270.bottom")}),-1.0]])]});
            var Q37;
            Q37=makeQuery(id+"F0.imprint","IMPRINT",FACE,{"disambiguationData":[TD([[makeQuery(id+"F0.imprint","IMPRINT",EDGE,{"derivedFrom":sQuery(id+"F0.wireOp",EDGE,"E271.bottom")}),-1.0]])]});
            var Q38;
            Q38=makeQuery(id+"F0.imprint","IMPRINT",FACE,{"disambiguationData":[TD([[makeQuery(id+"F0.imprint","IMPRINT",EDGE,{"derivedFrom":sQuery(id+"F0.wireOp",EDGE,"E275.MirrorCS")}),-1.0]])]});
            extrude(context, id + "F1", {"entities" : qUnion([Q0, Q1, Q2, Q3, Q4, Q5, Q6, Q7, Q8, Q9, Q10, Q11, Q12, Q13, Q14, Q15, Q16, Q17, Q18, Q19, Q20, Q21, Q22, Q23, Q24, Q25, Q26, Q27, Q28, Q29, Q30, Q31, Q32, Q33, Q34, Q35, Q36, Q37, Q38]), "depth" : 15.5 * mm});
        }
    });
